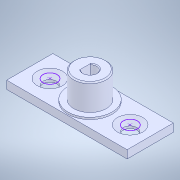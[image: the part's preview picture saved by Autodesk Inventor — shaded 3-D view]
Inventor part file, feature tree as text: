
AUTODESK INVENTOR PART (.ipt)
format: ipt  version: 2021 (Build 250183000, 183)  size: 170,496 bytes
history: native  units: in
note: dims shown in document units (in); Inventor stores cm internally (conversion verified against a paired STEP export)
features: sketch x5, extrude x4, chamfer x2, projected_geometry x2, hole x1, other x1
ambient origin geometry x8: Origin, YZ Plane, XZ Plane, XY Plane, X Axis, Y Axis, Z Axis, Center Point
bodies: Solid1 (feature_tree)
feature tree (15):
  extrude  "Extrusion1"  Depth=0.3937in TaperAngle=0.0deg
  extrude  "Extrusion2"  Depth=0.3937in TaperAngle=0.0deg
  extrude  "Extrusion3"  Depth=0.002in
  extrude  "Extrusion4"  Depth=0.3937in TaperAngle=45.0deg
  chamfer  "Chamfer1"  Distance=0.3937in
  hole  "Hole2"  [1 undecoded]
  chamfer  "Chamfer2"  [1 undecoded]
  sketch  "Sketch1"  dims[d1=0.3937in d2=0.0in d3=0.3937in d4=0.0in]
  projected_geometry  "Projected Loop1"
  sketch  "Sketch2"  dims[d5=0.002in d6=0.3937in d7=0.0in]
  sketch  "Sketch3"  dims[d8=0.0118in d9=0.0787in d10=45.0deg]
  sketch  "Sketch6"  dims[d19=0.1339in d20=0.2362in d21=0.248in d22=0.0787in d23=90.0deg d24=0.315in d25=0.0in d26=0.002in]
  sketch  "Sketch7"  dims[d27=0.002in d28=0.0079in d29=0.0787in d30=45.0deg d32=0.3937in d33=0.0in d34=0.0039in]
  projected_geometry  "Projected Loop2"
  other  "CSK for M4 Countersunk Flat Head Screw1"
note: 2 required parameter values undecoded (feature->parameter linkage not recoverable at this tier; creation-order binding heuristic only, values carry confidence <= 0.55)
